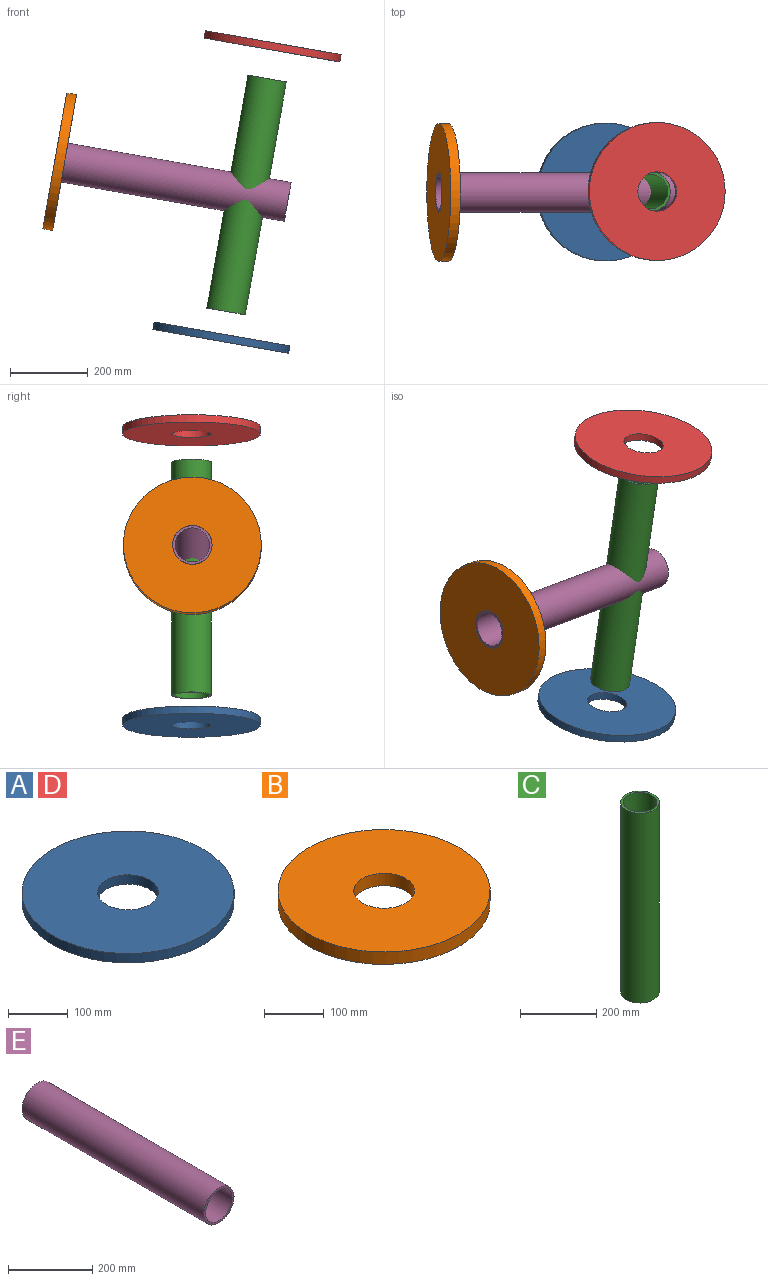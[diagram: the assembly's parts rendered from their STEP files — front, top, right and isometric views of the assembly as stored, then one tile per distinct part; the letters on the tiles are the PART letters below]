
ASSEMBLY  parts=5 mates=4
PART A: 4 faces, bbox 355.6x355.6x19.1 mm
  f0: cylinder r=50.8mm len=101.6mm, axis (0,0,-1), area 6080.5mm2, adj f2,f3
  f1: cylinder r=177.8mm len=355.6mm, axis (0,0,-1), area 21281.7mm2, adj f2,f3
  f2: plane 355.6x355.6mm, normal (0,0,1), area 91207.3mm2, adj f0,f1
  f3: plane 355.6x355.6mm, normal (0,0,-1), area 91207.3mm2, adj f0,f1
PART B: 4 faces, bbox 355.6x355.6x25.4 mm
  f0: cylinder r=50.8mm len=101.6mm, axis (0,0,-1), area 8107.3mm2, adj f2,f3
  f1: cylinder r=177.8mm len=355.6mm, axis (0,0,-1), area 28375.6mm2, adj f2,f3
  f2: plane 355.6x355.6mm, normal (0,0,1), area 91207.3mm2, adj f0,f1
  f3: plane 355.6x355.6mm, normal (0,0,-1), area 91207.3mm2, adj f0,f1
PART C: 4 faces, bbox 101.6x101.6x609.6 mm
  f0: cylinder r=44.45mm len=609.6mm, axis (0,0,-1), area 170253.7mm2, adj f2,f3
  f1: cylinder r=50.8mm len=609.6mm, axis (0,0,-1), area 194575.7mm2, adj f2,f3
  f2: plane 101.6x101.6mm, normal (0,0,1), area 1900.2mm2, adj f0,f1
  f3: plane 101.6x101.6mm, normal (0,0,-1), area 1900.2mm2, adj f0,f1
PART D: same geometry as A
PART E: 4 faces, bbox 101.6x609.6x101.6 mm
  f0: cylinder r=44.45mm len=609.6mm, axis (0,1,0), area 170253.7mm2, adj f2,f3
  f1: cylinder r=50.8mm len=609.6mm, axis (0,1,0), area 194575.7mm2, adj f2,f3
  f2: plane 101.6x101.6mm, normal (0,-1,0), area 1900.2mm2, adj f0,f1
  f3: plane 101.6x101.6mm, normal (0,1,0), area 1900.2mm2, adj f0,f1
PLACE A rot(axis=(-1,0,0.09),180deg) t=(-14.45,7.17,-389.97)mm
PLACE B rot(axis=(-0.02,-1,0.02),80deg) t=(-420.21,5.21,51.85)mm
PLACE C rot(axis=(-1,0,0.09),180deg) t=(48.75,7.17,-31.52)mm
PLACE D rot(axis=(0,1,0),10deg) t=(114.65,7.17,342.19)mm
PLACE E rot(axis=(-0.37,0.5,0.79),109.2deg) t=(-145.05,5.21,3.33)mm
MATE cylindrical D.f1 <-> C.f0  axis (0.17,0,0.98) through (117.96,7.17,360.96)mm
MATE cylindrical B.f1 <-> E.f1  axis (-0.98,0,0.17) through (-445.22,5.21,56.26)mm
MATE cylindrical A.f1 <-> C.f1  axis (0.17,0,0.98) through (-14.45,7.17,-389.97)mm
MATE planar B.f1 <-> E.f0  axis (-0.98,0,0.17) through (-445.22,5.21,56.26)mm
